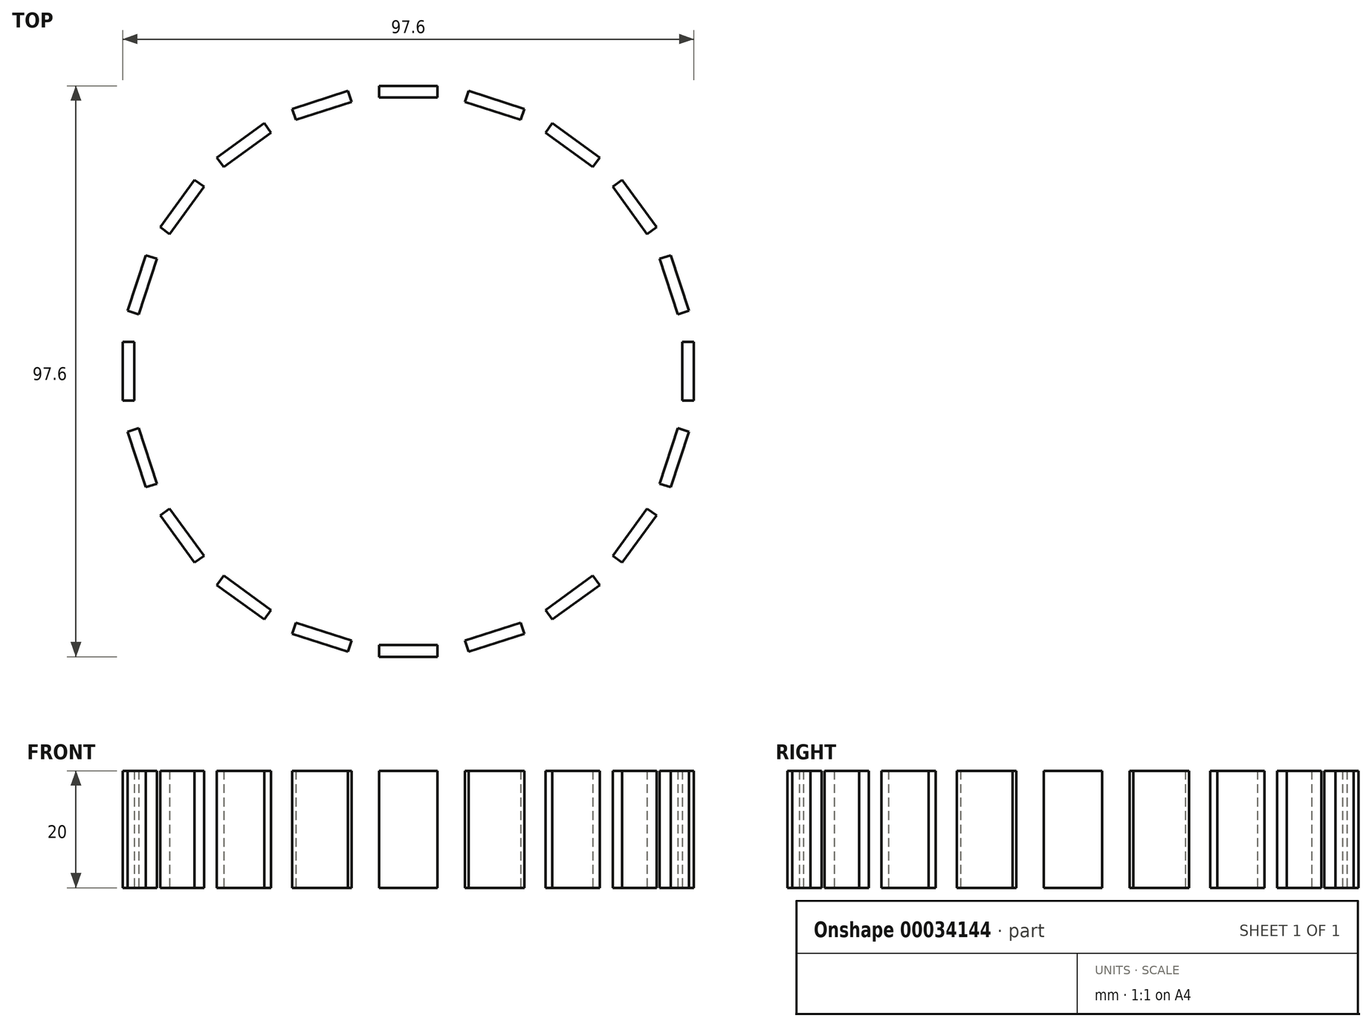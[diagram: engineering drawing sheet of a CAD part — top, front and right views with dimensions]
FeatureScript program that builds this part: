
annotation { "Feature Type Name" : "Feature", "Feature Type Description" : "" }
export const myFeature = defineFeature(function(context is Context, id is Id, definition is map)
    precondition{}
    {
        {
            var Q0;
            Q0=qCreatedBy(makeId("Right.planeOp"),FACE);
            cPlane(context, id + "F0", {"entities" : qUnion([Q0]), "cplaneType" : CPlaneType.OFFSET, "offset" : 48.8 * mm, "width" : 150 * mm, "height" : 150 * mm});
        }
        {
            var Q0;
            Q0=qCreatedBy(id+"F0.planeOp",FACE);
            var sketch = newSketch(context, id + "F1", { "sketchPlane" : qUnion([Q0])});
            skLineSegment(sketch, "E0.bottom", {"start": v(-5, 0) * mm, "end": v(5, 0) * mm});
            skLineSegment(sketch, "E0.top", {"start": v(-5, -20) * mm, "end": v(5, -20) * mm});
            skLineSegment(sketch, "E0.left", {"start": v(-5, 0) * mm, "end": v(-5, -20) * mm});
            skLineSegment(sketch, "E0.right", {"start": v(5, 0) * mm, "end": v(5, -20) * mm});
            skSolve(sketch);
        }
        {
            var Q0;
            Q0 = qSketchRegion(id + "F1", true);
            extrude(context, id + "F2", {"entities" : qUnion([Q0]), "oppositeDirection" : true, "depth" : 2 * mm});
        }
        {
            var Q0;
            Q0=qCreatedBy(makeId("Right.planeOp"),FACE);
            var sketch = newSketch(context, id + "F3", { "sketchPlane" : qUnion([Q0])});
            skLineSegment(sketch, "E1", {"start": v(0, -68.8) * mm, "end": v(0, 63.41) * mm, "construction": true});
            skSolve(sketch);
        }
        {
            var Q0;
            Q0=makeQuery(id+"F2.opExtrude","SWEPT_BODY",BODY,{"disambiguationData":[OSD([sQuery(id+"F1.wireOp",EDGE,"E0.bottom"),sQuery(id+"F1.wireOp",EDGE,"E0.top"),sQuery(id+"F1.wireOp",EDGE,"E0.left"),sQuery(id+"F1.wireOp",EDGE,"E0.right")])]});
            var Q1;
            Q1=sQuery(id+"F3.wireOp",EDGE,"E1");
            circularPattern(context, id + "F4", {"operationType" : NewBodyOperationType.ADD, "entities" : qUnion([Q0]), "axis" : qUnion([Q1]), "angle" : 360 * degree, "instanceCount" : 20, "equalSpace" : true});
        }
    });
